# Revit family: LV MARCUS BC
name_source: partatom
category: Aparatos sanitarios
revit_build: Autodesk Revit 2016 (Build: 20150220_1215(x64)
units: mm (PartAtom-declared; Revit-internal decimal feet)

## family parameters
Compartido = Sí
Corte con vacíos al cargar = No
Cota de conector redondo = Diámetro de uso
Número OmniClass = 23.45.05.14.14
Punto de cálculo de habitación = No
Se basa en plano de trabajo = Sí
Siempre vertical = Sí
Tipo de pieza = Normal
Título OmniClass = Sinks/Lavatories

## types (1)
- LV MARCUS BC
    Ceramic = Cerámica
    Comentarios de tipo = Lavabo Rectangular Marcus Bajo Cubierta con Rebosadero
    Descripción = Lavabo Rectangular Marcus Bajo Cubierta con Rebosadero
    Elevación por defecto = 0.0"
    Fabricante = Helvex S.A. de C.V.
    Materials = Cerámica al alto brillo
    Modelo = LV MARCUS BC
    Product Features = Lavabo Rectangular Marcus Bajo Cubierta con Rebosadero
    URL = https://www.helvex.com.mx
    Warranty = Helvex, S. A. de C. V. garantiza sus productos
cerámicos como libres de defectos en materiales y
procesos de fabricación por 30 años. En los herrajes
por defectos de manufactura por 5 años. En el
dispositivo TDS en el mingitorio seco por 3 años.
Tapa y asiento por un periodo de 2 años. La vigencia
de la garantía inicia a partir de la fecha de entrega
del producto al consumidor indicada en esta Póliza
de Garantía.

## geometry (parser evidence)
native form markers: Sweep x3
no freeform markers — native parametric forms only
